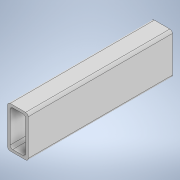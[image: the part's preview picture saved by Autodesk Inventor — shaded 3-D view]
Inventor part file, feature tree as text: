
AUTODESK INVENTOR PART (.ipt)
format: ipt  version: 2020 (Build 240168000, 168)  size: 120,320 bytes
history: native  units: in
note: dims shown in document units (in); Inventor stores cm internally (conversion verified against a paired STEP export)
features: extrude x1, sketch x1
ambient origin geometry x8: Origin, YZ Plane, XZ Plane, XY Plane, X Axis, Y Axis, Z Axis, Center Point
bodies: Solid1 (feature_tree)
feature tree (2):
  extrude  "Extrusion1"  Depth=1.0in
  sketch  "Sketch1"  dims[d0=2.0in d1=1.0in d2=0.125in d3=0.125in d4=0.125in d5=0.125in d6=0.125in d7=0.125in d8=0.125in d9=0.125in d10=0.125in d11=7.0in d12=0.0in]
